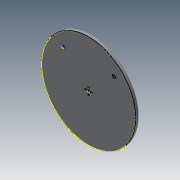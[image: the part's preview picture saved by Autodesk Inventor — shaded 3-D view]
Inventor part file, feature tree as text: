
AUTODESK INVENTOR PART (.ipt)
format: ipt  version: 2015 (Build 190159000, 159)  size: 105,984 bytes
history: native  units: mm
features: other x6, sketch x2, plane x1, extrude x1, projected_geometry x1
ambient origin geometry x8: Origin, YZ Plane, XZ Plane, XY Plane, X Axis, Y Axis, Z Axis, Center Point
bodies: Body1 (feature_tree)
feature tree (11):
  other  "Blocks"
  sketch  "Sketch1"  dims[d0=300.0mm d1=10.0mm]
  plane  "Work Plane1"
  extrude  "Extrusion4"  Depth=10.0mm
  sketch  "Sketch4"  dims[d2=10.0mm d7=105.0mm d8=40.0mm d9=4.0mm d10=40.0mm d12=360.0deg d18=10.0mm d26=10.0mm d27=0.0mm]
  other  "DXF"
  other  "Block1"
  projected_geometry  "Projected Loop1"
  other  "Block2"
  other  "Block2:1"
  other  "Block2:2"
